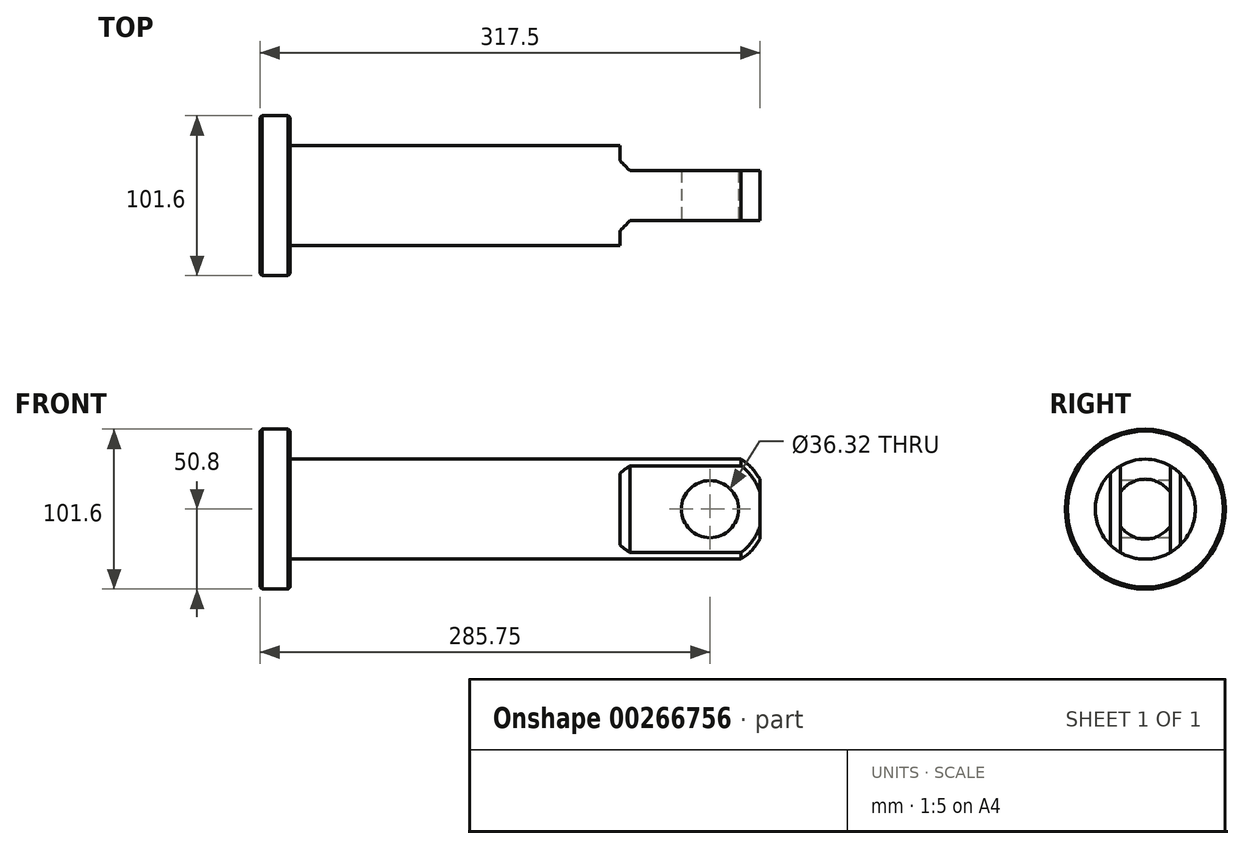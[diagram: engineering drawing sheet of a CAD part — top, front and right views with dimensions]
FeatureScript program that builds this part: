
annotation { "Feature Type Name" : "Feature", "Feature Type Description" : "" }
export const myFeature = defineFeature(function(context is Context, id is Id, definition is map)
    precondition{}
    {
        {
            var Q0;
            Q0=qCreatedBy(makeId("Front.planeOp"),FACE);
            var sketch = newSketch(context, id + "F0", { "sketchPlane" : qUnion([Q0])});
            skLineSegment(sketch, "E0", {"start": v(0, 0) * mm, "end": v(0, 19.05) * mm});
            skLineSegment(sketch, "E1", {"start": v(-11.94, 31.75) * mm, "end": v(-298.45, 31.75) * mm});
            skLineSegment(sketch, "E2", {"start": v(-298.45, 31.75) * mm, "end": v(-298.45, 50.8) * mm});
            skLineSegment(sketch, "E3", {"start": v(-298.45, 50.8) * mm, "end": v(-317.5, 50.8) * mm});
            skLineSegment(sketch, "E4", {"start": v(-317.5, 50.8) * mm, "end": v(-317.5, 0) * mm});
            skLineSegment(sketch, "E5", {"start": v(-317.5, 0) * mm, "end": v(0, 0) * mm});
            skLineSegment(sketch, "E6", {"start": v(21.69, 0) * mm, "end": v(-334.65, 0) * mm, "construction": true});
            skArc(sketch, "E7", {"start": v(0, 19.05) * mm, "mid": v(-5.23, 26.1) * mm, "end": v(-11.94, 31.75) * mm});
            skSolve(sketch);
        }
        {
            var Q0;
            Q0=makeQuery(id+"F0.imprint","IMPRINT",FACE,{"disambiguationData":[TD([[makeQuery(id+"F0.imprint","IMPRINT",EDGE,{"derivedFrom":sQuery(id+"F0.wireOp",EDGE,"E0")}),1.0]])]});
            var Q1;
            Q1=sQuery(id+"F0.wireOp",EDGE,"E6");
            revolve(context, id + "F1", {"entities" : qUnion([Q0]), "axis" : qUnion([Q1]), "revolveType" : RevolveType.FULL});
        }
        {
            var Q0;
            Q0=qCreatedBy(makeId("Top.planeOp"),FACE);
            var sketch = newSketch(context, id + "F2", { "sketchPlane" : qUnion([Q0])});
            skLineSegment(sketch, "E8.bottom", {"start": v(0, 15.87) * mm, "end": v(-88.9, 15.87) * mm});
            skLineSegment(sketch, "E8.top", {"start": v(0, 31.75) * mm, "end": v(-88.9, 31.75) * mm});
            skLineSegment(sketch, "E8.left", {"start": v(0, 15.87) * mm, "end": v(0, 31.75) * mm});
            skLineSegment(sketch, "E8.right", {"start": v(-88.9, 15.87) * mm, "end": v(-88.9, 31.75) * mm});
            skLineSegment(sketch, "E9.MirrorCS", {"start": v(0, -15.87) * mm, "end": v(-88.9, -15.87) * mm});
            skLineSegment(sketch, "E10.MirrorCS", {"start": v(0, -15.87) * mm, "end": v(0, -31.75) * mm});
            skLineSegment(sketch, "E11.MirrorCS", {"start": v(0, -31.75) * mm, "end": v(-88.9, -31.75) * mm});
            skLineSegment(sketch, "E12.MirrorCS", {"start": v(-88.9, -15.87) * mm, "end": v(-88.9, -31.75) * mm});
            skSolve(sketch);
        }
        {
            var Q0;
            Q0=makeQuery(id+"F2.imprint","IMPRINT",FACE,{"disambiguationData":[TD([[makeQuery(id+"F2.imprint","IMPRINT",EDGE,{"derivedFrom":sQuery(id+"F2.wireOp",EDGE,"E8.bottom")}),-1.0]])]});
            var Q1;
            Q1=makeQuery(id+"F2.imprint","IMPRINT",FACE,{"disambiguationData":[TD([[makeQuery(id+"F2.imprint","IMPRINT",EDGE,{"derivedFrom":sQuery(id+"F2.wireOp",EDGE,"E9.MirrorCS")}),1.0]])]});
            extrude(context, id + "F3", {"entities" : qUnion([Q0, Q1]), "operationType" : NewBodyOperationType.REMOVE, "endBound" : BoundingType.SYMMETRIC, "depth" : 63.5 * mm});
        }
        {
            var Q0;
            Q0=makeQuery(id+"F3.boolean.opBoolean","COPY",EDGE,{"derivedFrom":makeQuery(id+"F3.opExtrude","SWEPT_EDGE",EDGE,{"disambiguationData":[OSD([sQuery(id+"F2.wireOp",EDGE,"E9.MirrorCS"),sQuery(id+"F2.wireOp",EDGE,"E12.MirrorCS")])]})});
            var Q1;
            Q1=makeQuery(id+"F3.boolean.opBoolean","COPY",EDGE,{"derivedFrom":makeQuery(id+"F3.opExtrude","SWEPT_EDGE",EDGE,{"disambiguationData":[OSD([sQuery(id+"F2.wireOp",EDGE,"E8.bottom"),sQuery(id+"F2.wireOp",EDGE,"E8.right")])]})});
            chamfer(context, id + "F4", {"entities" : qUnion([Q0, Q1]), "width" : 6.35 * mm, "tangentPropagation" : true});
        }
        {
            var Q0;
            Q0=makeQuery(id+"F3.boolean.opBoolean","COPY",FACE,{"derivedFrom":makeQuery(id+"F3.opExtrude","SWEPT_FACE",FACE,{"disambiguationData":[OSD([sQuery(id+"F2.wireOp",EDGE,"E9.MirrorCS")])]})});
            var sketch = newSketch(context, id + "F5", { "sketchPlane" : qUnion([Q0])});
            skCircle(sketch, "E13", {"center": v(-31.75, 0) * mm, "radius": 18.16 * mm});
            skSolve(sketch);
        }
        {
            var Q0;
            Q0=makeQuery(id+"F5.imprint","IMPRINT",FACE,{"disambiguationData":[TD([[makeQuery(id+"F5.imprint","IMPRINT",EDGE,{"derivedFrom":sQuery(id+"F5.wireOp",EDGE,"E13")}),1.0]])]});
            extrude(context, id + "F6", {"entities" : qUnion([Q0]), "operationType" : NewBodyOperationType.REMOVE, "endBound" : BoundingType.THROUGH_ALL, "oppositeDirection" : true, "depth" : 25.4 * mm});
        }
        {
            var Q0;
            Q0=makeQuery(id+"F1.opRevolve","SWEPT_EDGE",EDGE,{"disambiguationData":[OSD([sQuery(id+"F0.wireOp",EDGE,"E2"),sQuery(id+"F0.wireOp",EDGE,"E3")])]});
            var Q1;
            Q1=makeQuery(id+"F1.opRevolve","SWEPT_EDGE",EDGE,{"disambiguationData":[OSD([sQuery(id+"F0.wireOp",EDGE,"E3"),sQuery(id+"F0.wireOp",EDGE,"E4")])]});
            chamfer(context, id + "F7", {"entities" : qUnion([Q0, Q1]), "width" : 1.27 * mm, "tangentPropagation" : true});
        }
    });
